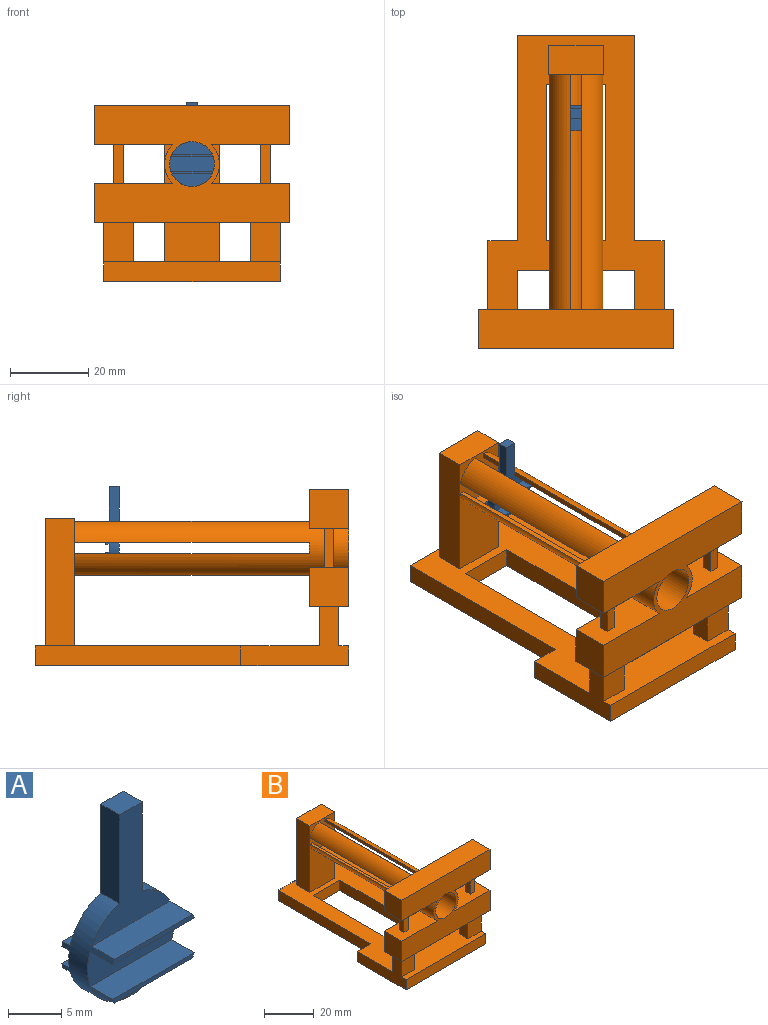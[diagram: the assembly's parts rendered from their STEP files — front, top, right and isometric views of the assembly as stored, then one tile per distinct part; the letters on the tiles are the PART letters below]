
ASSEMBLY  parts=2 mates=1
PART A: 22 faces, bbox 11.5x6.5x21.5 mm
  f0: cylinder r=5.75mm len=11.5mm, axis (0,1,0), area 91.3mm2, adj f1,f2,f3,f4,f5,f6,f7,f8
  f1: plane 11.5x2mm, normal (0,1,0), area 22.9mm2, adj f0,f14,f17
  f2: plane 11.1x4.25mm, normal (0,1,0), area 34.9mm2, adj f0,f16
  f3: plane 11.5x4mm, normal (0,-1,0), area 45.1mm2, adj f0,f7,f11
  f4: plane 13.25x10.36mm, normal (0,-1,0), area 54.3mm2, adj f0,f8,f19,f20,f21
  f5: plane 10.36x3.25mm, normal (0,-1,0), area 24.1mm2, adj f0,f10
  f6: plane 14.25x11.1mm, normal (0,1,0), area 65.1mm2, adj f0,f13,f19,f20,f21
  f7: plane 10.78x3mm, normal (0,0,-1), area 32.3mm2, adj f0,f3,f9
  f8: plane 10.36x3mm, normal (0,0,1), area 31.1mm2, adj f0,f4,f9
  f9: plane 10.78x0.5mm, normal (0,-1,0), area 5.3mm2, adj f0,f7,f8
  f10: plane 10.36x3mm, normal (0,0,-1), area 31.1mm2, adj f0,f5,f12
  f11: plane 10.78x3mm, normal (0,0,1), area 32.3mm2, adj f0,f3,f12
  f12: plane 10.78x0.5mm, normal (0,-1,0), area 5.3mm2, adj f0,f10,f11
  f13: plane 11.1x1mm, normal (0,0,1), area 11.1mm2, adj f0,f6,f15
  f14: plane 11.32x1mm, normal (0,0,-1), area 11.3mm2, adj f0,f1,f15
  f15: plane 11.32x0.5mm, normal (0,1,0), area 5.6mm2, adj f0,f13,f14
  f16: plane 11.1x1mm, normal (0,0,-1), area 11.1mm2, adj f0,f2,f18
  f17: plane 11.32x1mm, normal (0,0,1), area 11.3mm2, adj f0,f1,f18
  f18: plane 11.32x0.5mm, normal (0,1,0), area 5.6mm2, adj f0,f16,f17
  f19: plane 10.2x2.5mm, normal (-1,0,0), area 25.5mm2, adj f0,f4,f6,f21
  f20: plane 10.2x2.5mm, normal (1,0,0), area 25.5mm2, adj f0,f4,f6,f21
  f21: plane 3x2.5mm, normal (0,0,1), area 7.5mm2, adj f4,f6,f19,f20
PART B: 60 faces, bbox 50x80x45 mm
  f0: plane 3x1.45mm, normal (0,1,0), area 3.8mm2, adj f23,f24,f54,f58
  f1: plane 3x1.45mm, normal (0,1,0), area 3.8mm2, adj f23,f24,f56,f59
  f2: plane 32.5x14mm, normal (0,-1,0), area 416.3mm2, adj f4,f23,f24,f50,f52,f53,f54,f55
  f3: plane 50x10mm, normal (0,1,0), area 490.3mm2, adj f14,f15,f16,f17,f18,f23,f24,f55
  f4: plane 80x45mm, normal (0,0,1), area 1732.5mm2, adj f2,f5,f6,f7,f8,f9,f10,f11
  f5: plane 7.5x5mm, normal (0,1,0), area 37.5mm2, adj f4,f35,f37,f47
  f6: plane 15x5mm, normal (0,1,0), area 75mm2, adj f4,f37,f45,f46
  f7: plane 10x5mm, normal (1,0,0), area 50mm2, adj f4,f37,f41,f43
  f8: plane 10x5mm, normal (1,0,0), area 50mm2, adj f4,f9,f13,f36
  f9: plane 10x7.5mm, normal (0,-1,0), area 75mm2, adj f4,f8,f13,f35
  f10: plane 10x5mm, normal (-1,0,0), area 50mm2, adj f4,f37,f41,f43
  f11: plane 10x5mm, normal (-1,0,0), area 50mm2, adj f4,f12,f13,f38
  f12: plane 10x7.5mm, normal (0,-1,0), area 75mm2, adj f4,f11,f13,f39
  f13: plane 50x10mm, normal (0,0,-1), area 425mm2, adj f8,f9,f11,f12,f20,f21,f25,f26
  f14: plane 20.1x10mm, normal (0,0,-1), area 194.8mm2, adj f3,f15,f23,f25,f31,f32,f33,f34
  f15: plane 10x10mm, normal (1,0,0), area 100mm2, adj f3,f14,f16,f25
  f16: plane 50x10mm, normal (0,0,1), area 500mm2, adj f3,f15,f17,f25
  f17: plane 10x10mm, normal (-1,0,0), area 100mm2, adj f3,f16,f18,f25
  f18: plane 20.1x10mm, normal (0,0,-1), area 194.8mm2, adj f3,f17,f23,f25,f27,f28,f29,f30
  f19: plane 20.1x10mm, normal (0,0,1), area 194.8mm2, adj f20,f23,f25,f26,f27,f28,f29,f30
  f20: plane 10x10mm, normal (-1,0,0), area 100mm2, adj f13,f19,f25,f26
  f21: plane 10x10mm, normal (1,0,0), area 100mm2, adj f13,f22,f25,f26
  f22: plane 20.1x10mm, normal (0,0,1), area 194.8mm2, adj f21,f23,f25,f26,f31,f32,f33,f34
  f23: cylinder r=7mm len=70mm, axis (0,1,0), area 2317.5mm2, adj f0,f1,f2,f3,f14,f18,f19,f22
  f24: cylinder r=5.75mm len=70mm, axis (0,1,0), area 1982.7mm2, adj f0,f1,f2,f3,f25,f54,f55,f56
  f25: plane 50x30mm, normal (0,-1,0), area 1023.1mm2, adj f13,f14,f15,f16,f17,f18,f19,f20
  f26: plane 50x10mm, normal (0,1,0), area 486.5mm2, adj f13,f19,f20,f21,f22,f23
  f27: plane 10x2.5mm, normal (1,0,0), area 25mm2, adj f18,f19,f29,f30
  f28: plane 10x2.5mm, normal (-1,0,0), area 25mm2, adj f18,f19,f29,f30
  f29: plane 10x2.5mm, normal (0,-1,0), area 25mm2, adj f18,f19,f27,f28
  f30: plane 10x2.5mm, normal (0,1,0), area 25mm2, adj f18,f19,f27,f28
  f31: plane 10x2.5mm, normal (1,0,0), area 25mm2, adj f14,f22,f33,f34
  f32: plane 10x2.5mm, normal (-1,0,0), area 25mm2, adj f14,f22,f33,f34
  f33: plane 10x2.5mm, normal (0,-1,0), area 25mm2, adj f14,f22,f31,f32
  f34: plane 10x2.5mm, normal (0,1,0), area 25mm2, adj f14,f22,f31,f32
  f35: plane 27.5x15mm, normal (-1,0,0), area 187.5mm2, adj f4,f5,f9,f13,f36,f37,f42
  f36: plane 10x7.5mm, normal (0,1,0), area 75mm2, adj f4,f8,f13,f35
  f37: plane 80x45mm, normal (0,0,-1), area 1912.5mm2, adj f5,f6,f7,f10,f35,f39,f40,f41
  f38: plane 10x7.5mm, normal (0,1,0), area 75mm2, adj f4,f11,f13,f39
  f39: plane 27.5x15mm, normal (1,0,0), area 187.5mm2, adj f4,f12,f13,f37,f38,f40,f42
  f40: plane 7.5x5mm, normal (0,1,0), area 37.5mm2, adj f4,f37,f39,f44
  f41: plane 30x5mm, normal (0,1,0), area 150mm2, adj f4,f7,f10,f37
  f42: plane 45x5mm, normal (0,-1,0), area 225mm2, adj f4,f35,f37,f39
  f43: plane 30x5mm, normal (0,-1,0), area 150mm2, adj f4,f7,f10,f37
  f44: plane 52.5x5mm, normal (1,0,0), area 262.5mm2, adj f4,f37,f40,f49
  f45: plane 40x5mm, normal (-1,0,0), area 200mm2, adj f4,f6,f37,f48
  f46: plane 40x5mm, normal (1,0,0), area 200mm2, adj f4,f6,f37,f48
  f47: plane 52.5x5mm, normal (-1,0,0), area 262.5mm2, adj f4,f5,f37,f49
  f48: plane 15x5mm, normal (0,-1,0), area 75mm2, adj f4,f37,f45,f46
  f49: plane 30x5mm, normal (0,1,0), area 150mm2, adj f4,f37,f44,f47
  f50: plane 32.5x7.5mm, normal (1,0,0), area 243.7mm2, adj f2,f4,f51,f53
  f51: plane 32.5x14mm, normal (0,1,0), area 455mm2, adj f4,f50,f52,f53
  f52: plane 32.5x7.5mm, normal (-1,0,0), area 243.7mm2, adj f2,f4,f51,f53
  f53: plane 14x7.5mm, normal (0,0,1), area 105mm2, adj f2,f50,f51,f52
  f54: plane 60x1.29mm, normal (0,0,-1), area 77.2mm2, adj f0,f2,f23,f24
  f55: plane 60x1.29mm, normal (-1,0,0), area 77.2mm2, adj f2,f3,f23,f24
  f56: plane 60x1.29mm, normal (0,0,-1), area 77.2mm2, adj f1,f2,f23,f24
  f57: plane 60x1.29mm, normal (1,0,0), area 77.2mm2, adj f2,f3,f23,f24
  f58: plane 60x1.29mm, normal (0,0,1), area 77.2mm2, adj f0,f2,f23,f24
  f59: plane 60x1.29mm, normal (0,0,1), area 77.2mm2, adj f1,f2,f23,f24
PLACE A t=(-70.55,-79.44,35.62)mm
PLACE B t=(-70.55,-135.59,25.62)mm
MATE slider A.f0 <-> B.f23  axis (0,-1,0) through (-70.55,-79.44,35.62)mm
